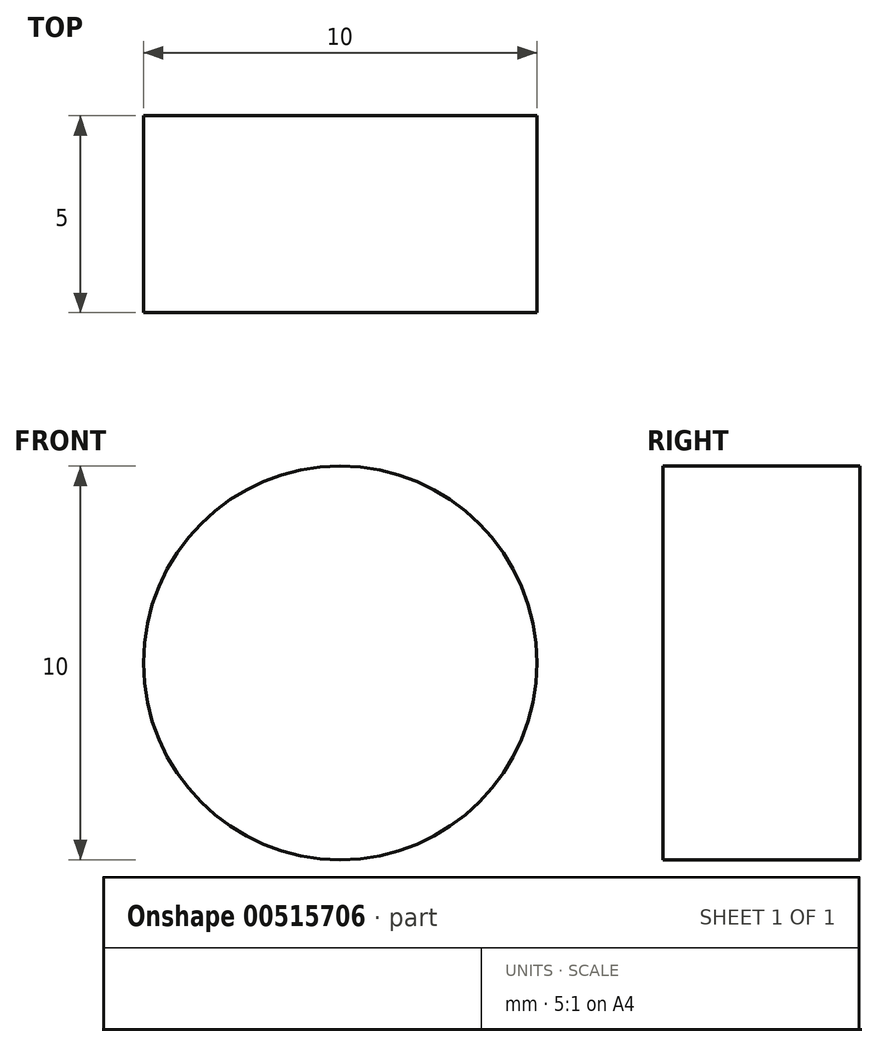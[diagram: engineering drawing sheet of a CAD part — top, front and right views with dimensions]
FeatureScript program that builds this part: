
annotation { "Feature Type Name" : "Feature", "Feature Type Description" : "" }
export const myFeature = defineFeature(function(context is Context, id is Id, definition is map)
    precondition{}
    {
        {
            var Q0;
            Q0=qCreatedBy(makeId("Front.planeOp"),FACE);
            var sketch = newSketch(context, id + "F0", { "sketchPlane" : qUnion([Q0])});
            skCircle(sketch, "E0", {"center": v(0, 0) * mm, "radius": 5 * mm});
            skSolve(sketch);
        }
        {
            var Q0;
            Q0 = qSketchRegion(id + "F0", true);
            extrude(context, id + "F1", {"entities" : qUnion([Q0]), "depth" : 5 * mm, "offsetDistance" : 25 * mm});
        }
    });
